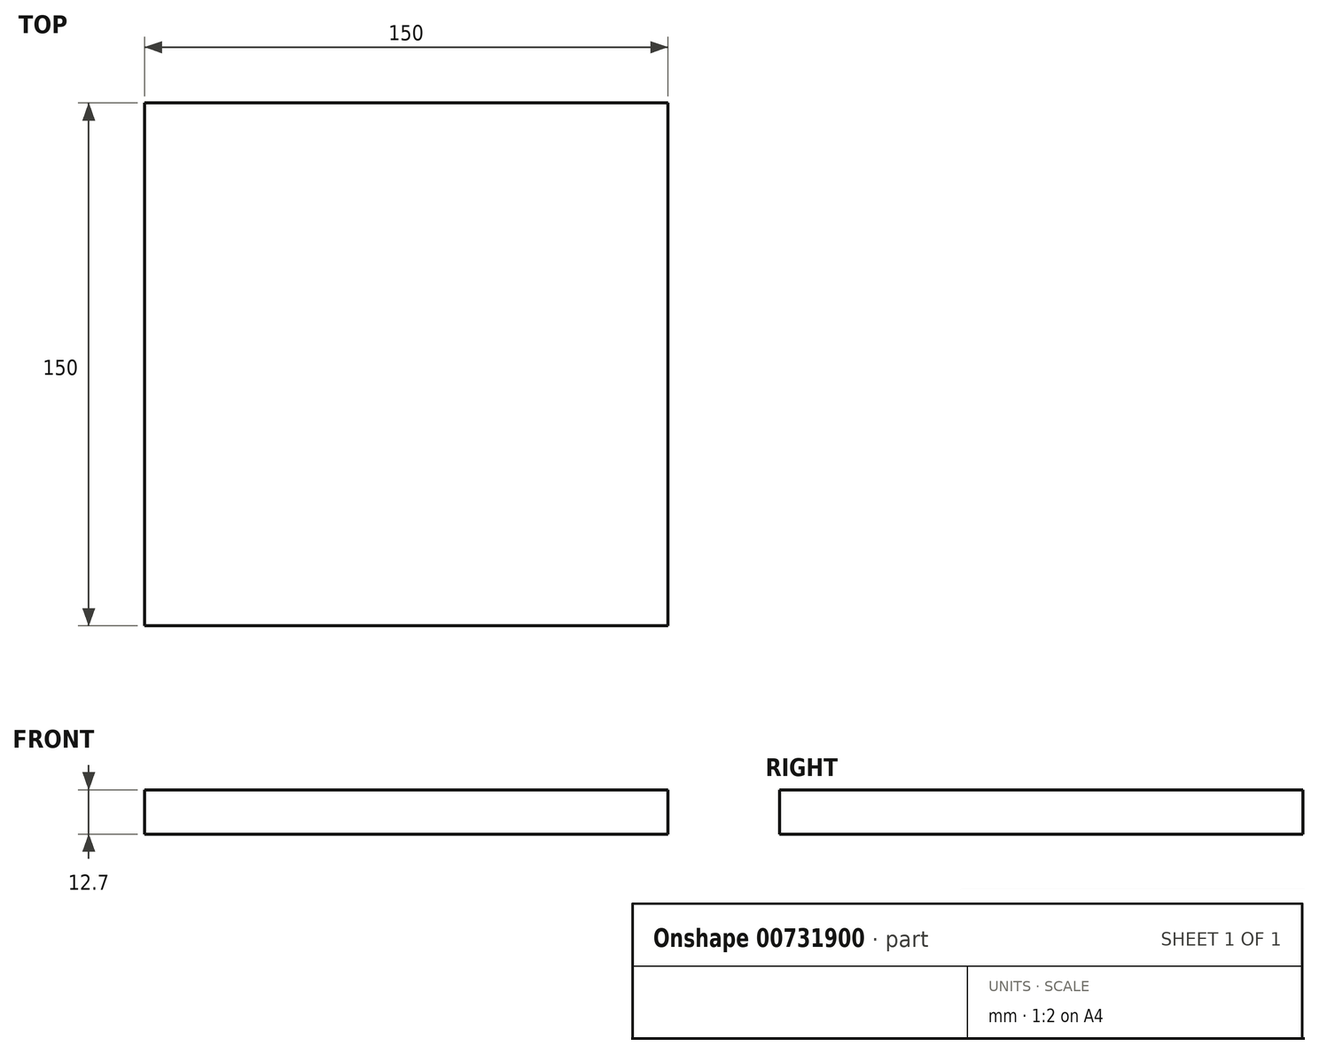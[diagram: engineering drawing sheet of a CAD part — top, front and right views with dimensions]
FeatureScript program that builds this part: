
annotation { "Feature Type Name" : "Feature", "Feature Type Description" : "" }
export const myFeature = defineFeature(function(context is Context, id is Id, definition is map)
    precondition{}
    {
        {
            var Q0;
            Q0=qCreatedBy(makeId("Top.planeOp"),FACE);
            var sketch = newSketch(context, id + "F0", { "sketchPlane" : qUnion([Q0])});
            skLineSegment(sketch, "E0.bottom", {"start": v(-75, 75) * mm, "end": v(75, 75) * mm});
            skLineSegment(sketch, "E0.top", {"start": v(-75, -75) * mm, "end": v(75, -75) * mm});
            skLineSegment(sketch, "E0.left", {"start": v(-75, 75) * mm, "end": v(-75, -75) * mm});
            skLineSegment(sketch, "E0.right", {"start": v(75, 75) * mm, "end": v(75, -75) * mm});
            skPoint(sketch, "E0.middle", {"position": v(0, 0) * mm});
            skSolve(sketch);
        }
        {
            var Q0;
            Q0=makeQuery(id+"F0.imprint","IMPRINT",FACE,{"disambiguationData":[TD([[makeQuery(id+"F0.imprint","IMPRINT",EDGE,{"derivedFrom":sQuery(id+"F0.wireOp",EDGE,"E0.bottom")}),-1.0]])]});
            extrude(context, id + "F1", {"entities" : qUnion([Q0]), "depth" : 12.7 * mm, "offsetDistance" : 25.4 * mm});
        }
    });
